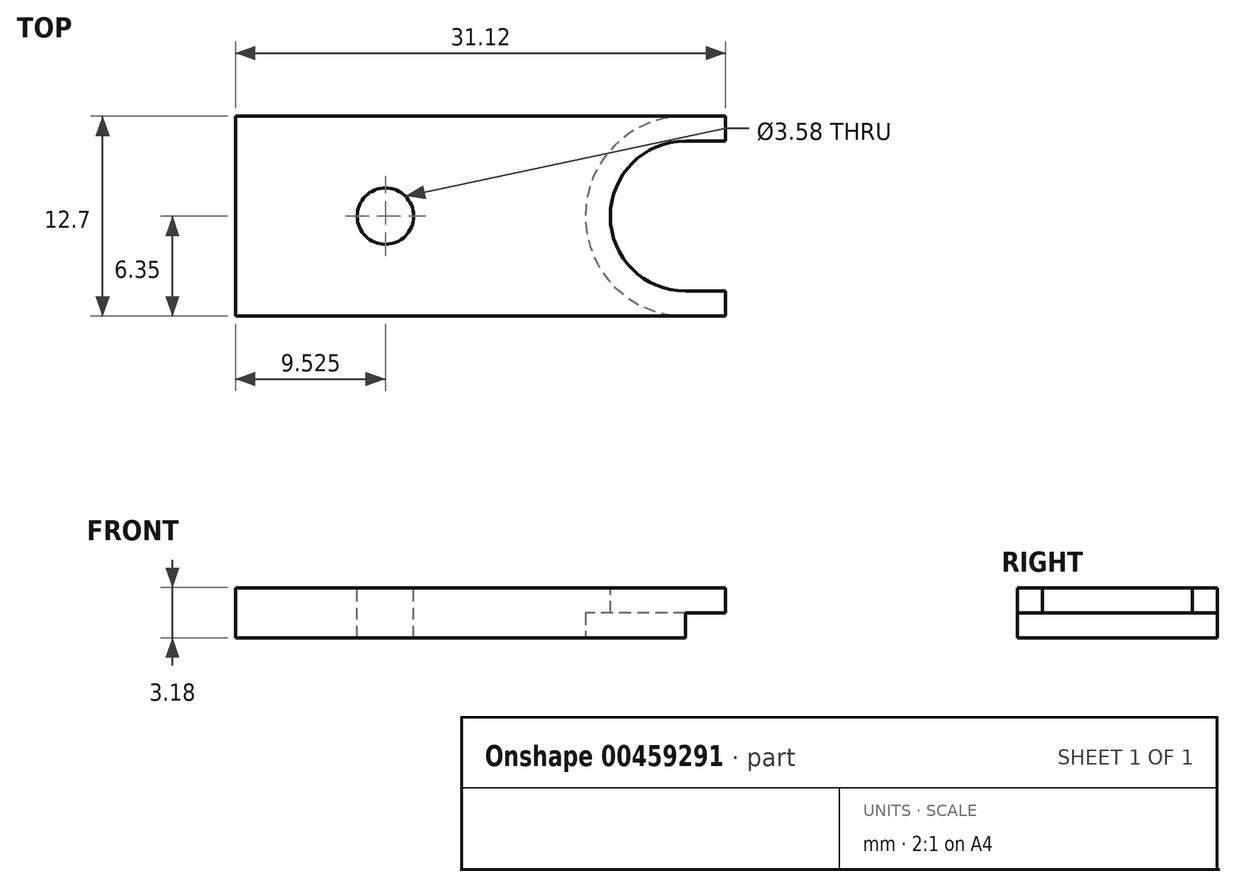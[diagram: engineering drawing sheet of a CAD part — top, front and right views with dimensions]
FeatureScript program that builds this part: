
annotation { "Feature Type Name" : "Feature", "Feature Type Description" : "" }
export const myFeature = defineFeature(function(context is Context, id is Id, definition is map)
    precondition{}
    {
        {
            var Q0;
            Q0=qCreatedBy(makeId("Front.planeOp"),FACE);
            var sketch = newSketch(context, id + "F0", { "sketchPlane" : qUnion([Q0])});
            skLineSegment(sketch, "E0.bottom", {"start": v(0, 0) * mm, "end": v(31.12, 0) * mm});
            skLineSegment(sketch, "E0.top", {"start": v(0, 3.18) * mm, "end": v(31.12, 3.18) * mm});
            skLineSegment(sketch, "E0.left", {"start": v(0, 0) * mm, "end": v(0, 3.18) * mm});
            skLineSegment(sketch, "E0.right", {"start": v(31.12, 0) * mm, "end": v(31.12, 3.18) * mm});
            skLineSegment(sketch, "E1", {"start": v(7.71, 4.67) * mm, "end": v(7.71, -3.78) * mm, "construction": true});
            skLineSegment(sketch, "E2", {"start": v(28.58, 5.08) * mm, "end": v(28.58, -3.78) * mm, "construction": true});
            skLineSegment(sketch, "E3", {"start": v(31.12, 1.59) * mm, "end": v(14.84, 1.59) * mm});
            skSolve(sketch);
        }
        {
            var Q0;
            {var subQ1=sQuery(id+"F0.wireOp",EDGE,"E0.bottom");Q0=makeQuery(id+"F0.imprint","IMPRINT",FACE,{"disambiguationData":[TD([[makeQuery(id+"F0.imprint","IMPRINT",EDGE,{"derivedFrom":subQ1}),1.0]])]});}
            extrude(context, id + "F1", {"entities" : qUnion([Q0]), "endBound" : BoundingType.SYMMETRIC, "depth" : 12.7 * mm});
        }
        {
            var Q0;
            Q0=makeQuery(id+"F1.opExtrude","SWEPT_FACE",FACE,{"disambiguationData":[OSD([sQuery(id+"F0.wireOp",EDGE,"E0.top")])]});
            var sketch = newSketch(context, id + "F2", { "sketchPlane" : qUnion([Q0])});
            skLineSegment(sketch, "E4", {"start": v(28.58, 7.93) * mm, "end": v(28.58, -9.16) * mm});
            skLineSegment(sketch, "E5", {"start": v(9.52, 5.17) * mm, "end": v(9.53, -9.24) * mm});
            skCircle(sketch, "E6", {"center": v(9.53, 0) * mm, "radius": 1.8 * mm});
            skLineSegment(sketch, "E7", {"start": v(23.81, 7.98) * mm, "end": v(23.81, 3.7) * mm});
            skLineSegment(sketch, "E8", {"start": v(23.81, 3.7) * mm, "end": v(23.81, -9.38) * mm});
            skLineSegment(sketch, "E9", {"start": v(22.23, -9.38) * mm, "end": v(22.23, 8.92) * mm});
            skLineSegment(sketch, "E10", {"start": v(26.06, -4.76) * mm, "end": v(31.12, -4.76) * mm});
            skLineSegment(sketch, "E11", {"start": v(27.1, 4.76) * mm, "end": v(31.12, 4.76) * mm});
            skArc(sketch, "E12", {"start": v(28.58, 6.35) * mm, "mid": v(22.23, 0) * mm, "end": v(28.58, -6.35) * mm});
            skArc(sketch, "E13", {"start": v(28.57, 4.76) * mm, "mid": v(23.81, 0) * mm, "end": v(28.58, -4.76) * mm});
            skSolve(sketch);
        }
        {
            var Q0;
            {var subQ0=sQuery(id+"F2.wireOp",EDGE,"E13");var subQ4=makeQuery(id+"F2.imprint","INTERSECT",VERTEX,{"derivedFrom":[sQuery(id+"F2.wireOp",EDGE,"E8"),subQ0]});Q0=makeQuery(id+"F2.imprint","IMPRINT",FACE,{"disambiguationData":[TD([[makeQuery(id+"F2.imprint","IMPRINT",EDGE,{"disambiguationData":[TD([[subQ4,1.0]])],"derivedFrom":subQ0}),1.0]])]});}
            var Q1;
            {var subQ0=sQuery(id+"F2.wireOp",EDGE,"E13");var subQ1=sQuery(id+"F2.wireOp",EDGE,"E11");var subQ2=sQuery(id+"F2.wireOp",EDGE,"E4");var subQ3=makeQuery(id+"F2.imprint","INTERSECT",VERTEX,{"derivedFrom":[subQ2,subQ1,subQ0]});Q1=makeQuery(id+"F2.imprint","IMPRINT",FACE,{"disambiguationData":[TD([[makeQuery(id+"F2.imprint","IMPRINT",EDGE,{"disambiguationData":[TD([[subQ3,-1.0]])],"derivedFrom":subQ2}),1.0]])]});}
            extrude(context, id + "F3", {"entities" : qUnion([Q0, Q1]), "operationType" : NewBodyOperationType.REMOVE, "endBound" : BoundingType.THROUGH_ALL, "oppositeDirection" : true, "depth" : 3.17 * mm});
        }
        {
            var Q0;
            Q0=makeQuery(id+"F1.opExtrude","SWEPT_FACE",FACE,{"disambiguationData":[OSD([sQuery(id+"F0.wireOp",EDGE,"E0.bottom")])]});
            var sketch = newSketch(context, id + "F4", { "sketchPlane" : qUnion([Q0])});
            skLineSegment(sketch, "E14", {"start": v(31.12, 6.35) * mm, "end": v(31.12, -5.56) * mm});
            skLineSegment(sketch, "E15", {"start": v(28.58, 7.37) * mm, "end": v(28.58, -8.1) * mm});
            skLineSegment(sketch, "E16", {"start": v(22.23, 8.46) * mm, "end": v(22.23, -10.44) * mm});
            skArc(sketch, "E17", {"start": v(28.57, 6.35) * mm, "mid": v(22.23, 0) * mm, "end": v(28.58, -6.35) * mm});
            skSolve(sketch);
        }
        {
            var Q0;
            {var subQ1=sQuery(id+"F0.wireOp",EDGE,"E0.bottom");var subQ4=makeQuery(id+"F1.opExtrude","SWEPT_FACE",FACE,{"disambiguationData":[OSD([subQ1])]});var subQ5=makeQuery(id+"F3.boolean.opBoolean","INTERSECT",EDGE,{"derivedFrom":[subQ4,makeQuery(id+"F3.opExtrude","SWEPT_FACE",FACE,{"disambiguationData":[OSD([sQuery(id+"F2.wireOp",EDGE,"E10")])]})]});Q0=makeQuery(id+"F4.imprint","IMPRINT",FACE,{"disambiguationData":[TD([[makeQuery(id+"F4.imprint","IMPRINT",EDGE,{"derivedFrom":subQ5}),1.0]])]});}
            var Q1;
            {var subQ2=sQuery(id+"F0.wireOp",EDGE,"E0.bottom");var subQ5=makeQuery(id+"F1.opExtrude","SWEPT_FACE",FACE,{"disambiguationData":[OSD([subQ2])]});var subQ6=makeQuery(id+"F3.boolean.opBoolean","INTERSECT",EDGE,{"derivedFrom":[subQ5,makeQuery(id+"F3.opExtrude","SWEPT_FACE",FACE,{"disambiguationData":[OSD([sQuery(id+"F2.wireOp",EDGE,"E13")])]})]});Q1=makeQuery(id+"F4.imprint","IMPRINT",FACE,{"disambiguationData":[TD([[makeQuery(id+"F4.imprint","IMPRINT",EDGE,{"derivedFrom":subQ6}),1.0]])]});}
            var Q2;
            {var subQ0=sQuery(id+"F0.wireOp",EDGE,"E0.bottom");var subQ1=makeQuery(id+"F1.opExtrude","SWEPT_FACE",FACE,{"disambiguationData":[OSD([subQ0])]});var subQ3=makeQuery(id+"F3.opExtrude","SWEPT_FACE",FACE,{"disambiguationData":[OSD([sQuery(id+"F2.wireOp",EDGE,"E11")])]});var subQ10=makeQuery(id+"F3.boolean.opBoolean","INTERSECT",EDGE,{"derivedFrom":[subQ1,subQ3]});Q2=makeQuery(id+"F4.imprint","IMPRINT",FACE,{"disambiguationData":[TD([[makeQuery(id+"F4.imprint","IMPRINT",EDGE,{"derivedFrom":subQ10}),-1.0]])]});}
            extrude(context, id + "F5", {"entities" : qUnion([Q0, Q1, Q2]), "operationType" : NewBodyOperationType.REMOVE, "oppositeDirection" : true, "depth" : 1.57 * mm});
        }
        {
            var Q0;
            Q0=makeQuery(id+"F1.opExtrude","SWEPT_FACE",FACE,{"disambiguationData":[OSD([sQuery(id+"F0.wireOp",EDGE,"E0.top")])]});
            var sketch = newSketch(context, id + "F6", { "sketchPlane" : qUnion([Q0])});
            skLineSegment(sketch, "E18", {"start": v(9.52, 11) * mm, "end": v(9.53, -11) * mm});
            skCircle(sketch, "E19", {"center": v(9.53, 0) * mm, "radius": 1.8 * mm});
            skSolve(sketch);
        }
        {
            var Q0;
            Q0=sQuery(id+"F6.wireOp",VERTEX,"E19.center");
            var Q1;
            Q1=makeQuery(id+"F1.opExtrude","SWEPT_BODY",BODY,{"disambiguationData":[OSD([sQuery(id+"F0.wireOp",EDGE,"E0.bottom"),sQuery(id+"F0.wireOp",EDGE,"E0.top"),sQuery(id+"F0.wireOp",EDGE,"E0.left"),sQuery(id+"F0.wireOp",EDGE,"E0.right")])]});
            hole(context, id + "F7", {"style" : HoleStyle.SIMPLE, "endStyle" : HoleEndStyle.THROUGH, "holeDiameter" : 3.58 * mm, "isTappedThrough" : true, "tappedDepth" : 7.14 * mm, "tapClearance" : 3, "startFromSketch" : true, "locations" : qUnion([Q0]), "scope" : qUnion([Q1])});
        }
    });
